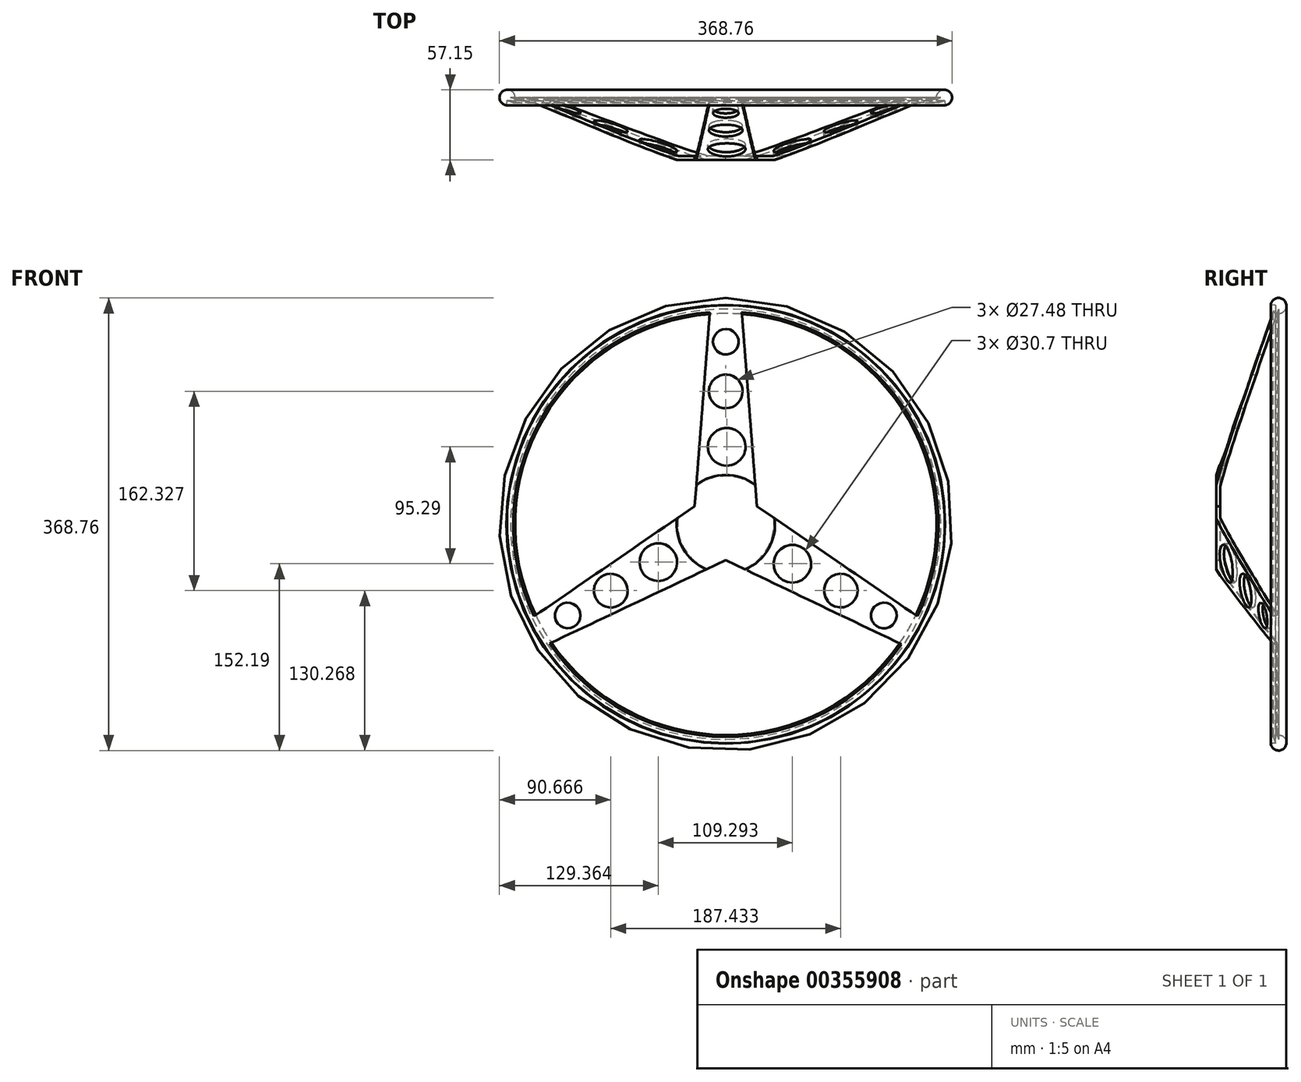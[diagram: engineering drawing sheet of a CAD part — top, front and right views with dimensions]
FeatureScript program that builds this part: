
annotation { "Feature Type Name" : "Feature", "Feature Type Description" : "" }
export const myFeature = defineFeature(function(context is Context, id is Id, definition is map)
    precondition{}
    {
        {
            var Q0;
            Q0=qCreatedBy(makeId("Front.planeOp"),FACE);
            var sketch = newSketch(context, id + "F0", { "sketchPlane" : qUnion([Q0])});
            skCircle(sketch, "E0", {"center": v(0, 0) * mm, "radius": 177.8 * mm});
            skLineSegment(sketch, "E1.1", {"start": v(139.7, -109.99) * mm, "end": v(141.28, -110.9) * mm});
            skLineSegment(sketch, "E2", {"start": v(-159.95, -77.64) * mm, "end": v(-25.4, 14.66) * mm});
            skLineSegment(sketch, "E3", {"start": v(-147.63, -99.09) * mm, "end": v(0, -29.33) * mm});
            skPoint(sketch, "E3.startSnap0", {"position": v(-147.63, -99.9) * mm});
            skLineSegment(sketch, "E4", {"start": v(159.95, -77.64) * mm, "end": v(25.4, 14.66) * mm});
            skLineSegment(sketch, "E5", {"start": v(0, -29.33) * mm, "end": v(147.22, -99.7) * mm});
            skLineSegment(sketch, "E6", {"start": v(-12.7, 177.8) * mm, "end": v(-25.4, 14.66) * mm});
            skLineSegment(sketch, "E7", {"start": v(12.74, 177.34) * mm, "end": v(25.4, 14.66) * mm});
            skPoint(sketch, "E8.1.end.orphan", {"position": v(-25.4, 177.8) * mm});
            skPoint(sketch, "E9.orphan", {"position": v(25.4, 177.8) * mm});
            skPoint(sketch, "E10.start.orphan", {"position": v(12.7, 177.8) * mm});
            skPoint(sketch, "E11.1.end.orphan", {"position": v(166.68, -66.9) * mm});
            skPoint(sketch, "E12.orphan", {"position": v(160.33, -77.9) * mm});
            skPoint(sketch, "E13.orphan", {"position": v(147.63, -99.9) * mm});
            skPoint(sketch, "E1.0.end.orphan", {"position": v(-141.28, -110.9) * mm});
            skPoint(sketch, "E14.orphan", {"position": v(-160.33, -77.9) * mm});
            skPoint(sketch, "E8.0.end.orphan", {"position": v(-166.68, -66.9) * mm});
            skPoint(sketch, "E15.end.orphan", {"position": v(0, 177.8) * mm});
            skPoint(sketch, "E16.end.orphan", {"position": v(-153.98, -88.9) * mm});
            skPoint(sketch, "E17.end.orphan", {"position": v(153.98, -88.9) * mm});
            skCircle(sketch, "E18", {"center": v(0, 0) * mm, "radius": 29.33 * mm});
            skSolve(sketch);
        }
        {
            var Q0;
            {var subQ0=sQuery(id+"F0.wireOp",EDGE,"E2");Q0=makeQuery(id+"F0.imprint","IMPRINT",FACE,{"disambiguationData":[TD([[makeQuery(id+"F0.imprint","IMPRINT",EDGE,{"derivedFrom":subQ0}),-1.0]])]});}
            var Q1;
            {var subQ0=sQuery(id+"F0.wireOp",EDGE,"E7");Q1=makeQuery(id+"F0.imprint","IMPRINT",FACE,{"disambiguationData":[TD([[makeQuery(id+"F0.imprint","IMPRINT",EDGE,{"derivedFrom":subQ0}),-1.0]])]});}
            var Q2;
            {var subQ0=sQuery(id+"F0.wireOp",EDGE,"E4");Q2=makeQuery(id+"F0.imprint","IMPRINT",FACE,{"disambiguationData":[TD([[makeQuery(id+"F0.imprint","IMPRINT",EDGE,{"derivedFrom":subQ0}),1.0]])]});}
            var Q3;
            {var subQ0=sQuery(id+"F0.wireOp",EDGE,"E18");var subQ1=makeQuery(id+"F0.imprint","INTERSECT",VERTEX,{"derivedFrom":[sQuery(id+"F0.wireOp",EDGE,"E2"),sQuery(id+"F0.wireOp",EDGE,"E6"),subQ0]});Q3=makeQuery(id+"F0.imprint","IMPRINT",FACE,{"disambiguationData":[TD([[makeQuery(id+"F0.imprint","IMPRINT",EDGE,{"disambiguationData":[TD([[subQ1,1.0]])],"derivedFrom":subQ0}),1.0]])]});}
            extrude(context, id + "F1", {"entities" : qUnion([Q0, Q1, Q2, Q3]), "depth" : 50.8 * mm});
        }
        {
            var Q0;
            Q0=qCreatedBy(makeId("Right.planeOp"),FACE);
            var sketch = newSketch(context, id + "F2", { "sketchPlane" : qUnion([Q0])});
            skCircle(sketch, "E19", {"center": v(0, 178.03) * mm, "radius": 6.35 * mm});
            skSolve(sketch);
        }
        {
            var Q0;
            Q0=qSketchRegion(id+"F2",true);
            var Q1;
            {var subQ0=sQuery(id+"F0.wireOp",EDGE,"E0");Q1=makeQuery(id+"F1.opExtrude","SWEPT_FACE",FACE,{"disambiguationData":[OSD([subQ0]),TDD([makeQuery(id+"F0.imprint","IMPRINT",EDGE,{"disambiguationData":[TD([[makeQuery(id+"F0.imprint","INTERSECT",VERTEX,{"derivedFrom":[subQ0,sQuery(id+"F0.wireOp",EDGE,"E7")]}),-1.0]])],"derivedFrom":subQ0})])]});}
            revolve(context, id + "F3", {"operationType" : NewBodyOperationType.ADD, "entities" : qUnion([Q0]), "axis" : qUnion([Q1]), "revolveType" : RevolveType.FULL});
        }
        {
            var Q0;
            Q0=qCreatedBy(makeId("Right.planeOp"),FACE);
            var sketch = newSketch(context, id + "F4", { "sketchPlane" : qUnion([Q0])});
            skLineSegment(sketch, "E20", {"start": v(0, 178.42) * mm, "end": v(-2.42, 178.42) * mm});
            skLineSegment(sketch, "E21", {"start": v(-2.42, 178.42) * mm, "end": v(-50.73, 40.03) * mm});
            skLineSegment(sketch, "E22", {"start": v(-50.73, 40.03) * mm, "end": v(-69.71, 57.98) * mm});
            skLineSegment(sketch, "E23", {"start": v(-69.71, 57.98) * mm, "end": v(-64.88, 183.6) * mm});
            skLineSegment(sketch, "E24", {"start": v(-64.88, 183.6) * mm, "end": v(-2.42, 178.42) * mm});
            skLineSegment(sketch, "E25", {"start": v(0, 175.31) * mm, "end": v(-47.51, 39.22) * mm});
            skLineSegment(sketch, "E26", {"start": v(-47.51, 39.22) * mm, "end": v(-47.51, 0) * mm});
            skLineSegment(sketch, "E27", {"start": v(-47.51, 0) * mm, "end": v(0, 0) * mm});
            skLineSegment(sketch, "E28", {"start": v(0, 0) * mm, "end": v(0, 175.31) * mm});
            skSolve(sketch);
        }
        {
            var Q0;
            Q0=makeQuery(id+"F1.opExtrude","CAP_FACE",FACE,{"disambiguationData":[OSD([sQuery(id+"F0.wireOp",EDGE,"E0"),sQuery(id+"F0.wireOp",EDGE,"E2"),sQuery(id+"F0.wireOp",EDGE,"E3"),sQuery(id+"F0.wireOp",EDGE,"E4"),sQuery(id+"F0.wireOp",EDGE,"E5"),sQuery(id+"F0.wireOp",EDGE,"E6"),sQuery(id+"F0.wireOp",EDGE,"E7")])],"isStart":true});
            var sketch = newSketch(context, id + "F5", { "sketchPlane" : qUnion([Q0])});
            skCircle(sketch, "E29", {"center": v(0, 0) * mm, "radius": 27.58 * mm});
            skSolve(sketch);
        }
        {
            var Q0;
            Q0=qSketchRegion(id+"F5",true);
            extrude(context, id + "F6", {"entities" : qUnion([Q0]), "operationType" : NewBodyOperationType.REMOVE, "oppositeDirection" : true, "depth" : 44.45 * mm});
        }
        {
            var Q0;
            Q0=qSketchRegion(id+"F4",true);
            var Q1;
            Q1=makeQuery(id+"F3.opRevolve","SWEPT_FACE",FACE,{"disambiguationData":[OSD([sQuery(id+"F2.wireOp",EDGE,"E19")])]});
            revolve(context, id + "F7", {"operationType" : NewBodyOperationType.REMOVE, "entities" : qUnion([Q0]), "axis" : qUnion([Q1]), "revolveType" : RevolveType.FULL, "oppositeDirection" : true});
        }
        {
            var Q0;
            Q0=qCreatedBy(makeId("Front.planeOp"),FACE);
            var sketch = newSketch(context, id + "F8", { "sketchPlane" : qUnion([Q0])});
            skCircle(sketch, "E30", {"center": v(0, 0) * mm, "radius": 38.86 * mm});
            skCircle(sketch, "E31", {"center": v(54.28, -32.19) * mm, "radius": 15.35 * mm});
            skCircle(sketch, "E32", {"center": v(93.72, -54.1) * mm, "radius": 13.74 * mm});
            skCircle(sketch, "E33", {"center": v(128.78, -74.37) * mm, "radius": 10.42 * mm});
            skCircle(sketch, "E34.1.1", {"center": v(0.74, 63.1) * mm, "radius": 15.35 * mm});
            skCircle(sketch, "E34.1.2", {"center": v(0, 108.21) * mm, "radius": 13.74 * mm});
            skCircle(sketch, "E34.1.3", {"center": v(0.02, 148.71) * mm, "radius": 10.42 * mm});
            skCircle(sketch, "E34.2.1", {"center": v(-55.02, -30.91) * mm, "radius": 15.35 * mm});
            skCircle(sketch, "E34.2.2", {"center": v(-93.71, -54.11) * mm, "radius": 13.74 * mm});
            skCircle(sketch, "E34.2.3", {"center": v(-128.8, -74.34) * mm, "radius": 10.42 * mm});
            skSolve(sketch);
        }
        {
            var Q0;
            Q0=makeQuery(id+"F8.imprint","IMPRINT",FACE,{"disambiguationData":[TD([[makeQuery(id+"F8.imprint","IMPRINT",EDGE,{"derivedFrom":sQuery(id+"F8.wireOp",EDGE,"E34.1.3")}),1.0]])]});
            var Q1;
            Q1=makeQuery(id+"F8.imprint","IMPRINT",FACE,{"disambiguationData":[TD([[makeQuery(id+"F8.imprint","IMPRINT",EDGE,{"derivedFrom":sQuery(id+"F8.wireOp",EDGE,"E34.1.2")}),1.0]])]});
            var Q2;
            Q2=makeQuery(id+"F8.imprint","IMPRINT",FACE,{"disambiguationData":[TD([[makeQuery(id+"F8.imprint","IMPRINT",EDGE,{"derivedFrom":sQuery(id+"F8.wireOp",EDGE,"E34.1.1")}),1.0]])]});
            var Q3;
            Q3=makeQuery(id+"F8.imprint","IMPRINT",FACE,{"disambiguationData":[TD([[makeQuery(id+"F8.imprint","IMPRINT",EDGE,{"derivedFrom":sQuery(id+"F8.wireOp",EDGE,"E34.2.3")}),1.0]])]});
            var Q4;
            Q4=makeQuery(id+"F8.imprint","IMPRINT",FACE,{"disambiguationData":[TD([[makeQuery(id+"F8.imprint","IMPRINT",EDGE,{"derivedFrom":sQuery(id+"F8.wireOp",EDGE,"E34.2.2")}),1.0]])]});
            var Q5;
            Q5=makeQuery(id+"F8.imprint","IMPRINT",FACE,{"disambiguationData":[TD([[makeQuery(id+"F8.imprint","IMPRINT",EDGE,{"derivedFrom":sQuery(id+"F8.wireOp",EDGE,"E34.2.1")}),1.0]])]});
            var Q6;
            Q6=makeQuery(id+"F8.imprint","IMPRINT",FACE,{"disambiguationData":[TD([[makeQuery(id+"F8.imprint","IMPRINT",EDGE,{"derivedFrom":sQuery(id+"F8.wireOp",EDGE,"E31")}),1.0]])]});
            var Q7;
            Q7=makeQuery(id+"F8.imprint","IMPRINT",FACE,{"disambiguationData":[TD([[makeQuery(id+"F8.imprint","IMPRINT",EDGE,{"derivedFrom":sQuery(id+"F8.wireOp",EDGE,"E32")}),1.0]])]});
            var Q8;
            Q8=makeQuery(id+"F8.imprint","IMPRINT",FACE,{"disambiguationData":[TD([[makeQuery(id+"F8.imprint","IMPRINT",EDGE,{"derivedFrom":sQuery(id+"F8.wireOp",EDGE,"E33")}),1.0]])]});
            extrude(context, id + "F9", {"entities" : qUnion([Q0, Q1, Q2, Q3, Q4, Q5, Q6, Q7, Q8]), "operationType" : NewBodyOperationType.REMOVE, "endBound" : BoundingType.THROUGH_ALL, "depth" : 25.4 * mm});
        }
    });
